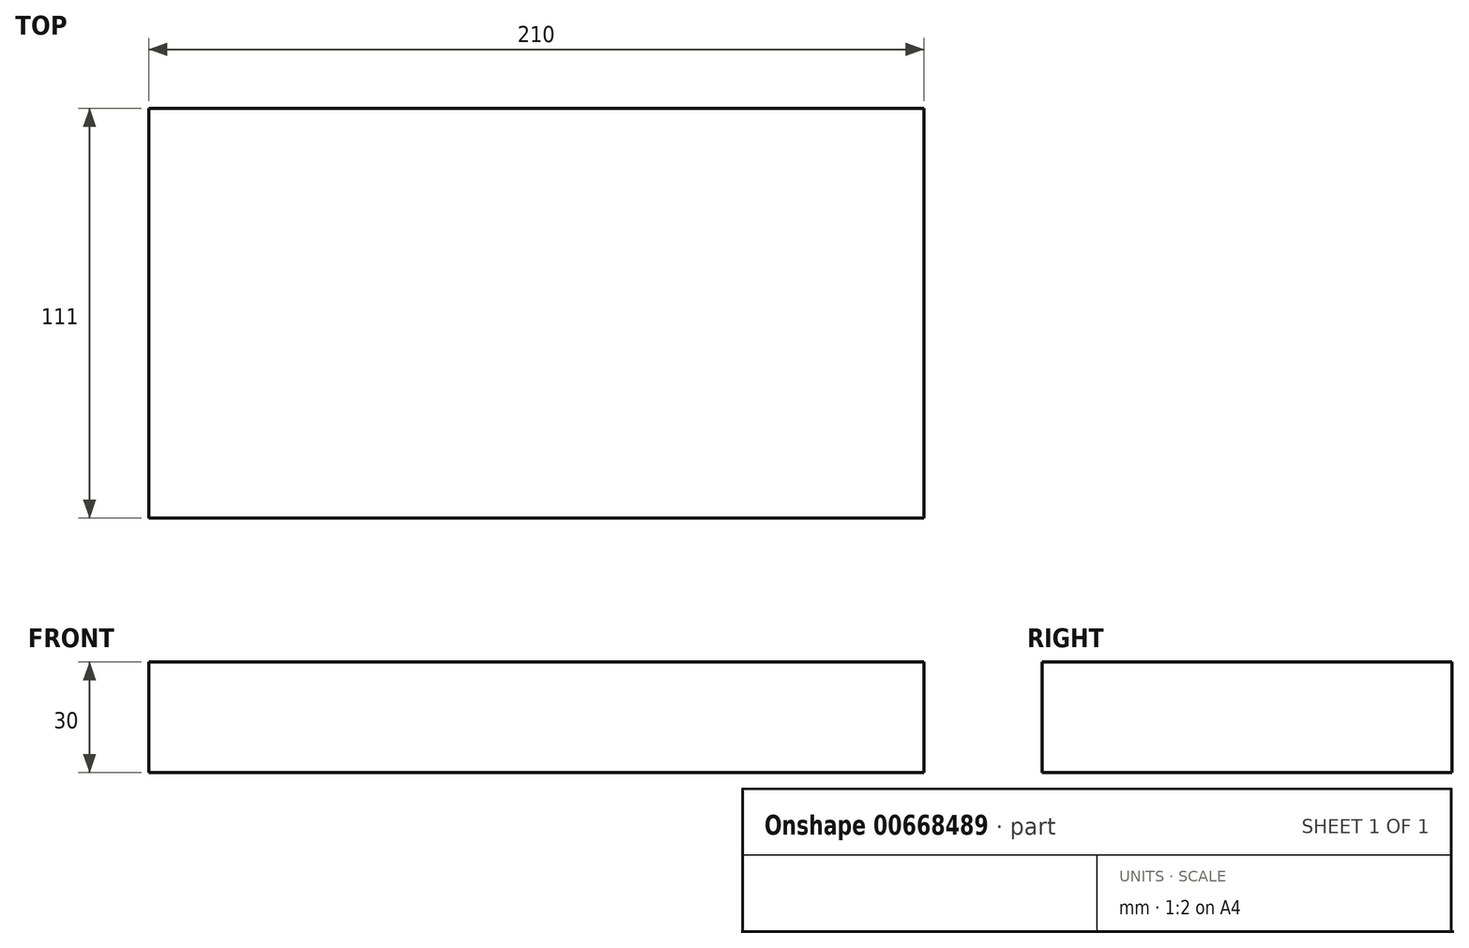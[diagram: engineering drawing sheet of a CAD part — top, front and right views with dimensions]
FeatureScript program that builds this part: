
annotation { "Feature Type Name" : "Feature", "Feature Type Description" : "" }
export const myFeature = defineFeature(function(context is Context, id is Id, definition is map)
    precondition{}
    {
        {
            var Q0;
            Q0=qCreatedBy(makeId("Top.planeOp"),FACE);
            var sketch = newSketch(context, id + "F0", { "sketchPlane" : qUnion([Q0])});
            skLineSegment(sketch, "E0.bottom", {"start": v(105, 55.5) * mm, "end": v(-105, 55.5) * mm});
            skLineSegment(sketch, "E0.top", {"start": v(105, -55.5) * mm, "end": v(-105, -55.5) * mm});
            skLineSegment(sketch, "E0.left", {"start": v(105, 55.5) * mm, "end": v(105, -55.5) * mm});
            skLineSegment(sketch, "E0.right", {"start": v(-105, 55.5) * mm, "end": v(-105, -55.5) * mm});
            skPoint(sketch, "E0.middle", {"position": v(0, 0) * mm});
            skSolve(sketch);
        }
        {
            var Q0;
            Q0=makeQuery(id+"F0.imprint","IMPRINT",FACE,{"disambiguationData":[TD([[makeQuery(id+"F0.imprint","IMPRINT",EDGE,{"derivedFrom":sQuery(id+"F0.wireOp",EDGE,"E0.bottom")}),1.0]])]});
            extrude(context, id + "F1", {"entities" : qUnion([Q0]), "depth" : 30 * mm, "offsetDistance" : 25 * mm});
        }
    });
